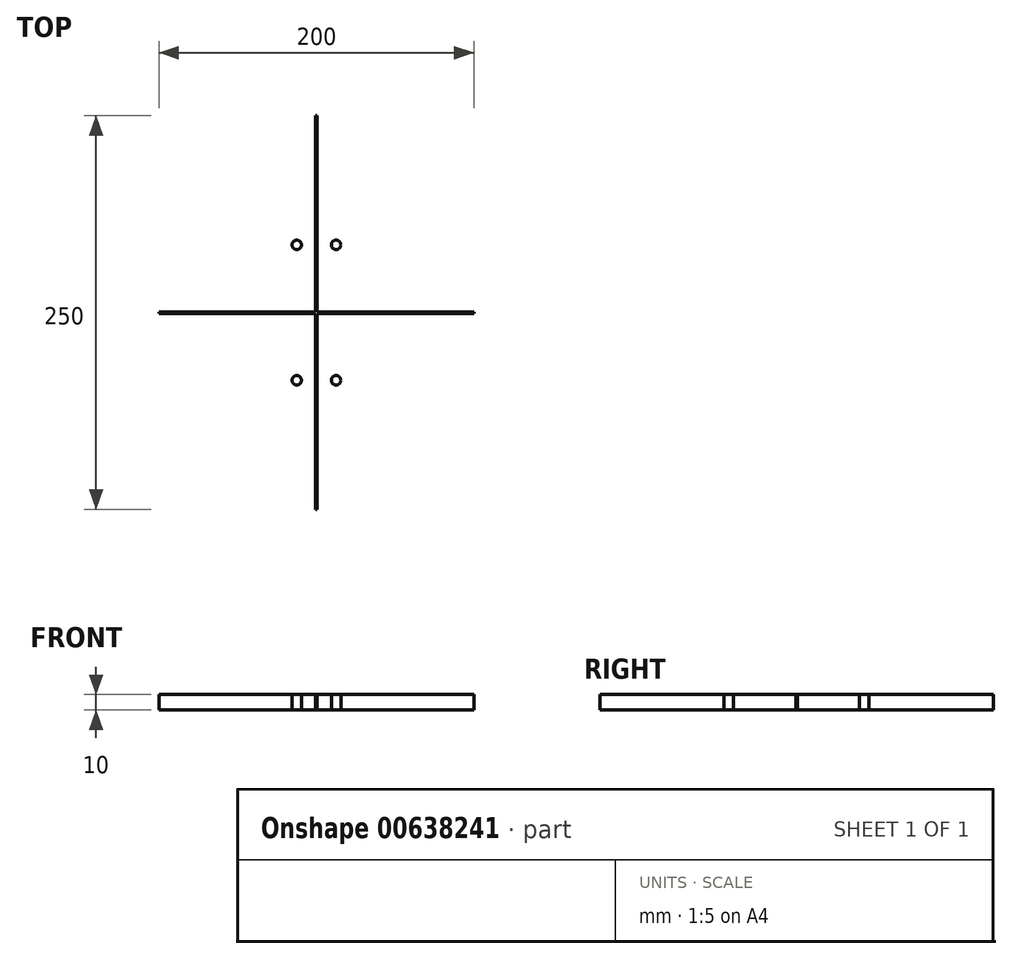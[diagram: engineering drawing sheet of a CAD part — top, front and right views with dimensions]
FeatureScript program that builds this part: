
annotation { "Feature Type Name" : "Feature", "Feature Type Description" : "" }
export const myFeature = defineFeature(function(context is Context, id is Id, definition is map)
    precondition{}
    {
        {
            var Q0;
            Q0=qCreatedBy(makeId("Top.planeOp"),FACE);
            var sketch = newSketch(context, id + "F0", { "sketchPlane" : qUnion([Q0])});
            skCircle(sketch, "E0", {"center": v(-12.5, 43) * mm, "radius": 3 * mm});
            skLineSegment(sketch, "E1", {"start": v(0, 0) * mm, "end": v(0, 100) * mm});
            skLineSegment(sketch, "E2.MirrorCS", {"start": v(0, -100) * mm, "end": v(0, 0) * mm});
            skLineSegment(sketch, "E3", {"start": v(0, 0) * mm, "end": v(-100, 0) * mm});
            skLineSegment(sketch, "E4.MirrorCS", {"start": v(0, 0) * mm, "end": v(100, 0) * mm});
            skLineSegment(sketch, "E5.bottom", {"start": v(-0.5, 125) * mm, "end": v(0.5, 125) * mm});
            skLineSegment(sketch, "E5.top", {"start": v(-0.5, -125) * mm, "end": v(0.5, -125) * mm});
            skLineSegment(sketch, "E5.left", {"start": v(-0.5, 125) * mm, "end": v(-0.5, -125) * mm});
            skLineSegment(sketch, "E5.right", {"start": v(0.5, 125) * mm, "end": v(0.5, -125) * mm});
            skPoint(sketch, "E5.middle", {"position": v(0, 0) * mm});
            skLineSegment(sketch, "E6.bottom", {"start": v(-100, 0.5) * mm, "end": v(100, 0.5) * mm});
            skLineSegment(sketch, "E6.top", {"start": v(-100, -0.5) * mm, "end": v(100, -0.5) * mm});
            skLineSegment(sketch, "E6.left", {"start": v(-100, 0.5) * mm, "end": v(-100, -0.5) * mm});
            skLineSegment(sketch, "E6.right", {"start": v(100, 0.5) * mm, "end": v(100, -0.5) * mm});
            skCircle(sketch, "E7.MirrorC", {"center": v(-12.5, -43) * mm, "radius": 3 * mm});
            skCircle(sketch, "E8.MirrorC", {"center": v(12.5, 43) * mm, "radius": 3 * mm});
            skCircle(sketch, "E9.MirrorC", {"center": v(12.5, -43) * mm, "radius": 3 * mm});
            skSolve(sketch);
        }
        {
            var Q0;
            Q0=qSketchRegion(id+"F0",true);
            extrude(context, id + "F1", {"entities" : qUnion([Q0]), "depth" : 10 * mm, "offsetDistance" : 25 * mm});
        }
    });
